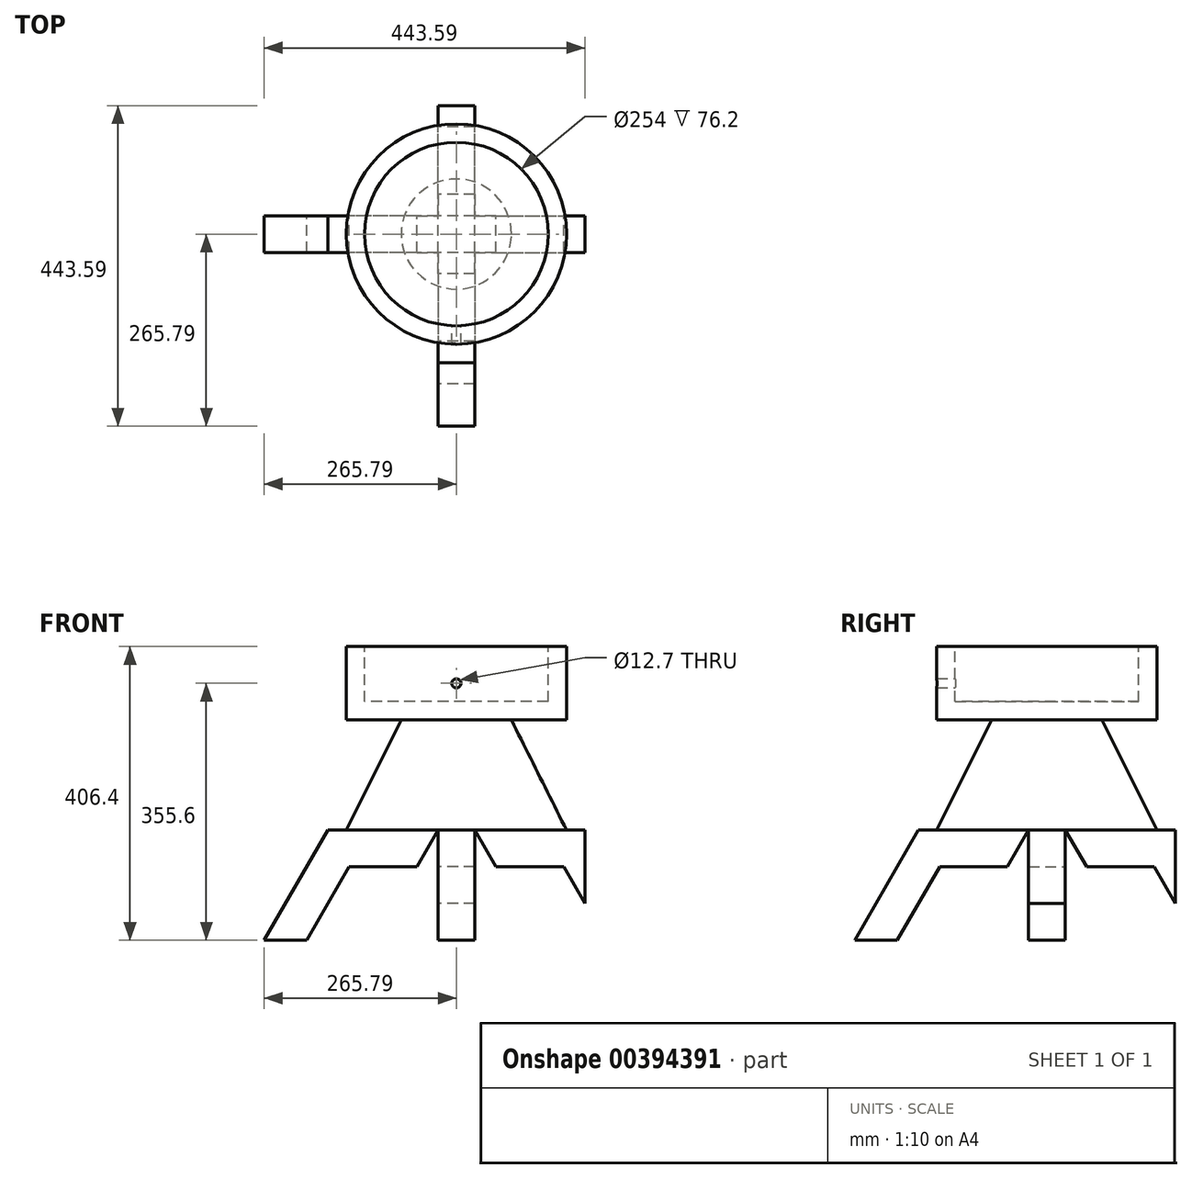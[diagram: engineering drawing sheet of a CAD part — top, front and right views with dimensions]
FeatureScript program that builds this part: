
annotation { "Feature Type Name" : "Feature", "Feature Type Description" : "" }
export const myFeature = defineFeature(function(context is Context, id is Id, definition is map)
    precondition{}
    {
        {
            var Q0;
            Q0=qCreatedBy(makeId("Front.planeOp"),FACE);
            var sketch = newSketch(context, id + "F0", { "sketchPlane" : qUnion([Q0])});
            skLineSegment(sketch, "E0", {"start": v(0, 0) * mm, "end": v(25.4, 0) * mm});
            skLineSegment(sketch, "E1", {"start": v(25.4, 0) * mm, "end": v(25.4, -50.8) * mm});
            skLineSegment(sketch, "E2", {"start": v(25.4, -50.8) * mm, "end": v(54.73, -50.8) * mm});
            skLineSegment(sketch, "E3", {"start": v(54.73, -50.8) * mm, "end": v(25.4, 0) * mm});
            skLineSegment(sketch, "E4", {"start": v(25.4, 0) * mm, "end": v(177.8, 0) * mm});
            skLineSegment(sketch, "E5", {"start": v(177.8, 0) * mm, "end": v(177.8, -152.4) * mm});
            skLineSegment(sketch, "E6", {"start": v(54.73, -50.8) * mm, "end": v(239.68, -50.8) * mm});
            skLineSegment(sketch, "E7", {"start": v(177.8, -152.4) * mm, "end": v(265.79, -152.4) * mm});
            skLineSegment(sketch, "E8", {"start": v(265.79, -152.4) * mm, "end": v(265.79, -152.4) * mm});
            skLineSegment(sketch, "E9", {"start": v(177.8, 0) * mm, "end": v(265.79, -152.4) * mm});
            skLineSegment(sketch, "E10", {"start": v(265.79, -152.4) * mm, "end": v(207.13, -152.4) * mm});
            skLineSegment(sketch, "E11", {"start": v(207.13, -50.8) * mm, "end": v(148.47, -50.8) * mm});
            skLineSegment(sketch, "E12", {"start": v(148.47, -50.8) * mm, "end": v(207.13, -152.4) * mm});
            skLineSegment(sketch, "E13", {"start": v(0, 0) * mm, "end": v(0, 26.22) * mm});
            skLineSegment(sketch, "E14.MirrorCS", {"start": v(-177.8, 0) * mm, "end": v(-265.79, -152.4) * mm});
            skLineSegment(sketch, "E15.MirrorCS", {"start": v(-265.79, -152.4) * mm, "end": v(-207.13, -152.4) * mm});
            skLineSegment(sketch, "E16.MirrorCS", {"start": v(-148.47, -50.8) * mm, "end": v(-207.13, -152.4) * mm});
            skLineSegment(sketch, "E17.MirrorCS", {"start": v(-54.73, -50.8) * mm, "end": v(-239.68, -50.8) * mm});
            skLineSegment(sketch, "E18.MirrorCS", {"start": v(-54.73, -50.8) * mm, "end": v(-25.4, 0) * mm});
            skLineSegment(sketch, "E19.MirrorCS", {"start": v(-25.4, 0) * mm, "end": v(-177.8, 0) * mm});
            skLineSegment(sketch, "E20.MirrorCS", {"start": v(0, 0) * mm, "end": v(-25.4, 0) * mm});
            skSolve(sketch);
        }
        {
            var Q0;
            Q0=qCreatedBy(makeId("Right.planeOp"),FACE);
            var sketch = newSketch(context, id + "F1", { "sketchPlane" : qUnion([Q0])});
            skLineSegment(sketch, "E21", {"start": v(0, 0) * mm, "end": v(25.4, 0) * mm});
            skLineSegment(sketch, "E22", {"start": v(25.4, 0) * mm, "end": v(25.4, -50.8) * mm});
            skLineSegment(sketch, "E23", {"start": v(25.4, -50.8) * mm, "end": v(54.73, -50.8) * mm});
            skLineSegment(sketch, "E24", {"start": v(54.73, -50.8) * mm, "end": v(25.4, 0) * mm});
            skLineSegment(sketch, "E25", {"start": v(25.4, 0) * mm, "end": v(177.8, 0) * mm});
            skLineSegment(sketch, "E26", {"start": v(177.8, 0) * mm, "end": v(177.8, -152.4) * mm});
            skLineSegment(sketch, "E27", {"start": v(54.73, -50.8) * mm, "end": v(282.95, -50.8) * mm});
            skLineSegment(sketch, "E28", {"start": v(177.8, -152.4) * mm, "end": v(265.79, -152.4) * mm});
            skLineSegment(sketch, "E29", {"start": v(222.52, -152.4) * mm, "end": v(265.79, -152.4) * mm});
            skLineSegment(sketch, "E30", {"start": v(177.8, 0) * mm, "end": v(265.79, -152.4) * mm});
            skLineSegment(sketch, "E31", {"start": v(265.79, -152.4) * mm, "end": v(207.13, -152.4) * mm});
            skLineSegment(sketch, "E32", {"start": v(207.13, -50.8) * mm, "end": v(148.47, -50.8) * mm});
            skLineSegment(sketch, "E33", {"start": v(148.47, -50.8) * mm, "end": v(207.13, -152.4) * mm});
            skLineSegment(sketch, "E34", {"start": v(0, 0) * mm, "end": v(0, 88.49) * mm});
            skLineSegment(sketch, "E35.MirrorCS", {"start": v(-177.8, 0) * mm, "end": v(-265.79, -152.4) * mm});
            skLineSegment(sketch, "E36.MirrorCS", {"start": v(-265.79, -152.4) * mm, "end": v(-207.13, -152.4) * mm});
            skLineSegment(sketch, "E37.MirrorCS", {"start": v(-148.47, -50.8) * mm, "end": v(-207.13, -152.4) * mm});
            skLineSegment(sketch, "E38.MirrorCS", {"start": v(-54.73, -50.8) * mm, "end": v(-282.95, -50.8) * mm});
            skLineSegment(sketch, "E39.MirrorCS", {"start": v(-54.73, -50.8) * mm, "end": v(-25.4, 0) * mm});
            skLineSegment(sketch, "E40.MirrorCS", {"start": v(-25.4, 0) * mm, "end": v(-177.8, 0) * mm});
            skLineSegment(sketch, "E41.MirrorCS", {"start": v(0, 0) * mm, "end": v(-25.4, 0) * mm});
            skSolve(sketch);
        }
        {
            var Q0;
            {var subQ0=sQuery(id+"F0.wireOp",EDGE,"E18.MirrorCS");Q0=makeQuery(id+"F0.imprint","IMPRINT",FACE,{"disambiguationData":[TD([[makeQuery(id+"F0.imprint","IMPRINT",EDGE,{"derivedFrom":subQ0}),1.0]])]});}
            var Q1;
            {var subQ0=sQuery(id+"F0.wireOp",EDGE,"E15.MirrorCS");Q1=makeQuery(id+"F0.imprint","IMPRINT",FACE,{"disambiguationData":[TD([[makeQuery(id+"F0.imprint","IMPRINT",EDGE,{"derivedFrom":subQ0}),1.0]])]});}
            var Q2;
            {var subQ5=sQuery(id+"F0.wireOp",EDGE,"E3");Q2=makeQuery(id+"F0.imprint","IMPRINT",FACE,{"disambiguationData":[TD([[makeQuery(id+"F0.imprint","IMPRINT",EDGE,{"derivedFrom":subQ5}),-1.0]])]});}
            var Q3;
            {var subQ5=sQuery(id+"F0.wireOp",EDGE,"E10");Q3=makeQuery(id+"F0.imprint","IMPRINT",FACE,{"disambiguationData":[TD([[makeQuery(id+"F0.imprint","IMPRINT",EDGE,{"derivedFrom":subQ5}),-1.0]])]});}
            var Q4;
            {var subQ0=sQuery(id+"F0.wireOp",EDGE,"E9");var subQ3=sQuery(id+"F0.wireOp",EDGE,"E11");var subQ5=makeQuery(id+"F0.imprint","INTERSECT",VERTEX,{"derivedFrom":[subQ0,subQ3]});Q4=makeQuery(id+"F0.imprint","IMPRINT",FACE,{"disambiguationData":[TD([[makeQuery(id+"F0.imprint","IMPRINT",EDGE,{"disambiguationData":[TD([[subQ5,-1.0]])],"derivedFrom":subQ3}),-1.0]])]});}
            var Q5;
            {var subQ0=sQuery(id+"F0.wireOp",EDGE,"E12");var subQ1=sQuery(id+"F0.wireOp",EDGE,"E5");var subQ2=makeQuery(id+"F0.imprint","INTERSECT",VERTEX,{"derivedFrom":[subQ1,subQ0]});Q5=makeQuery(id+"F0.imprint","IMPRINT",FACE,{"disambiguationData":[TD([[makeQuery(id+"F0.imprint","IMPRINT",EDGE,{"disambiguationData":[TD([[subQ2,1.0]])],"derivedFrom":subQ1}),-1.0]])]});}
            extrude(context, id + "F2", {"entities" : qUnion([Q0, Q1, Q2, Q3, Q4, Q5]), "endBound" : BoundingType.SYMMETRIC, "depth" : 50.8 * mm});
        }
        {
            var Q0;
            {var subQ6=sQuery(id+"F1.wireOp",EDGE,"E24");Q0=makeQuery(id+"F1.imprint","IMPRINT",FACE,{"disambiguationData":[TD([[makeQuery(id+"F1.imprint","IMPRINT",EDGE,{"derivedFrom":subQ6}),-1.0]])]});}
            var Q1;
            {var subQ0=sQuery(id+"F1.wireOp",EDGE,"E30");var subQ3=sQuery(id+"F1.wireOp",EDGE,"E32");var subQ5=makeQuery(id+"F1.imprint","INTERSECT",VERTEX,{"derivedFrom":[subQ0,subQ3]});Q1=makeQuery(id+"F1.imprint","IMPRINT",FACE,{"disambiguationData":[TD([[makeQuery(id+"F1.imprint","IMPRINT",EDGE,{"disambiguationData":[TD([[subQ5,-1.0]])],"derivedFrom":subQ3}),-1.0]])]});}
            var Q2;
            {var subQ0=sQuery(id+"F1.wireOp",EDGE,"E33");var subQ1=sQuery(id+"F1.wireOp",EDGE,"E26");var subQ2=makeQuery(id+"F1.imprint","INTERSECT",VERTEX,{"derivedFrom":[subQ1,subQ0]});Q2=makeQuery(id+"F1.imprint","IMPRINT",FACE,{"disambiguationData":[TD([[makeQuery(id+"F1.imprint","IMPRINT",EDGE,{"disambiguationData":[TD([[subQ2,1.0]])],"derivedFrom":subQ1}),-1.0]])]});}
            var Q3;
            {var subQ1=sQuery(id+"F1.wireOp",EDGE,"E31");var subQ3=makeQuery(id+"F1.imprint","IMPRINT",VERTEX,{"derivedFrom":subQ1});Q3=makeQuery(id+"F1.imprint","IMPRINT",FACE,{"disambiguationData":[TD([[makeQuery(id+"F1.imprint","IMPRINT",EDGE,{"disambiguationData":[TD([[subQ3,1.0]])],"derivedFrom":subQ1}),-1.0]])]});}
            var Q4;
            {var subQ0=sQuery(id+"F1.wireOp",EDGE,"E39.MirrorCS");Q4=makeQuery(id+"F1.imprint","IMPRINT",FACE,{"disambiguationData":[TD([[makeQuery(id+"F1.imprint","IMPRINT",EDGE,{"derivedFrom":subQ0}),1.0]])]});}
            var Q5;
            {var subQ0=sQuery(id+"F1.wireOp",EDGE,"E36.MirrorCS");Q5=makeQuery(id+"F1.imprint","IMPRINT",FACE,{"disambiguationData":[TD([[makeQuery(id+"F1.imprint","IMPRINT",EDGE,{"derivedFrom":subQ0}),1.0]])]});}
            extrude(context, id + "F3", {"entities" : qUnion([Q0, Q1, Q2, Q3, Q4, Q5]), "endBound" : BoundingType.SYMMETRIC, "depth" : 50.8 * mm});
        }
        {
            var Q0;
            Q0=qCreatedBy(makeId("Top.planeOp"),FACE);
            var sketch = newSketch(context, id + "F4", { "sketchPlane" : qUnion([Q0])});
            skCircle(sketch, "E42", {"center": v(0, 0) * mm, "radius": 152.4 * mm});
            skSolve(sketch);
        }
        {
            var Q0;
            Q0=makeQuery(id+"F4.imprint","IMPRINT",FACE,{"disambiguationData":[TD([[makeQuery(id+"F4.imprint","IMPRINT",EDGE,{"derivedFrom":sQuery(id+"F4.wireOp",EDGE,"E42")}),1.0]])]});
            cPlane(context, id + "F5", {"entities" : qUnion([Q0]), "cplaneType" : CPlaneType.OFFSET, "offset" : 152.4 * mm, "width" : 152.4 * mm, "height" : 152.4 * mm});
        }
        {
            var Q0;
            Q0=qCreatedBy(id+"F5.planeOp",FACE);
            var sketch = newSketch(context, id + "F6", { "sketchPlane" : qUnion([Q0])});
            skCircle(sketch, "E43", {"center": v(0, 0) * mm, "radius": 76.2 * mm});
            skSolve(sketch);
        }
        {
            var Q0;
            Q0=makeQuery(id+"F4.imprint","IMPRINT",FACE,{"disambiguationData":[TD([[makeQuery(id+"F4.imprint","IMPRINT",EDGE,{"derivedFrom":sQuery(id+"F4.wireOp",EDGE,"E42")}),1.0]])]});
            var Q1;
            Q1=makeQuery(id+"F6.imprint","IMPRINT",FACE,{"disambiguationData":[TD([[makeQuery(id+"F6.imprint","IMPRINT",EDGE,{"derivedFrom":sQuery(id+"F6.wireOp",EDGE,"E43")}),1.0]])]});
            loft(context, id + "F7", {"sheetProfilesArray" : [{ "sheetProfileEntities" : qUnion([Q0]) }, { "sheetProfileEntities" : qUnion([Q1]) }]});
        }
        {
            var Q0;
            Q0=makeQuery(id+"F7.opLoft","CAP_FACE",FACE,{"disambiguationData":[OSD([makeQuery(id+"F6.imprint","IMPRINT",FACE,{"disambiguationData":[TD([[makeQuery(id+"F6.imprint","IMPRINT",EDGE,{"derivedFrom":sQuery(id+"F6.wireOp",EDGE,"E43")}),1.0]])]})])],"isStart":true});
            var sketch = newSketch(context, id + "F8", { "sketchPlane" : qUnion([Q0])});
            skCircle(sketch, "E44", {"center": v(0, 0) * mm, "radius": 152.4 * mm});
            skSolve(sketch);
        }
        {
            var Q0;
            Q0=makeQuery(id+"F8.imprint","IMPRINT",FACE,{"disambiguationData":[TD([[makeQuery(id+"F8.imprint","IMPRINT",EDGE,{"derivedFrom":sQuery(id+"F8.wireOp",EDGE,"E44")}),1.0]])]});
            var Q1;
            Q1=makeQuery(id+"F8.imprint","IMPRINT",FACE,{"disambiguationData":[TD([[makeQuery(id+"F8.imprint","IMPRINT",EDGE,{"derivedFrom":makeQuery(id+"F7.opLoft","MID_CAP_EDGE",EDGE,{"disambiguationData":[OSD([sQuery(id+"F4.wireOp",EDGE,"E42"),sQuery(id+"F6.wireOp",EDGE,"E43")])],"capPos":1.0})}),1.0]])]});
            extrude(context, id + "F9", {"entities" : qUnion([Q0, Q1]), "operationType" : NewBodyOperationType.ADD, "depth" : 101.6 * mm});
        }
        {
            var Q0;
            Q0=makeQuery(id+"F9.opExtrude","CAP_FACE",FACE,{"disambiguationData":[OSD([sQuery(id+"F8.wireOp",EDGE,"E44")])],"isStart":false});
            var sketch = newSketch(context, id + "F10", { "sketchPlane" : qUnion([Q0])});
            skCircle(sketch, "E45", {"center": v(0, 0) * mm, "radius": 127 * mm});
            skSolve(sketch);
        }
        {
            var Q0;
            Q0=makeQuery(id+"F10.imprint","IMPRINT",FACE,{"disambiguationData":[TD([[makeQuery(id+"F10.imprint","IMPRINT",EDGE,{"derivedFrom":sQuery(id+"F10.wireOp",EDGE,"E45")}),1.0]])]});
            extrude(context, id + "F11", {"entities" : qUnion([Q0]), "operationType" : NewBodyOperationType.REMOVE, "oppositeDirection" : true, "depth" : 76.2 * mm});
        }
        {
            var Q0;
            Q0=qCreatedBy(makeId("Front.planeOp"),FACE);
            var sketch = newSketch(context, id + "F12", { "sketchPlane" : qUnion([Q0])});
            skLineSegment(sketch, "E46", {"start": v(0, 0) * mm, "end": v(0, 203.2) * mm});
            skCircle(sketch, "E47", {"center": v(0, 203.2) * mm, "radius": 6.35 * mm});
            skSolve(sketch);
        }
        {
            var Q0;
            Q0=makeQuery(id+"F12.imprint","IMPRINT",FACE,{"disambiguationData":[TD([[makeQuery(id+"F12.imprint","IMPRINT",EDGE,{"derivedFrom":sQuery(id+"F12.wireOp",EDGE,"E47")}),1.0]])]});
            extrude(context, id + "F13", {"entities" : qUnion([Q0]), "operationType" : NewBodyOperationType.REMOVE, "endBound" : BoundingType.THROUGH_ALL, "depth" : 25.4 * mm});
        }
    });
